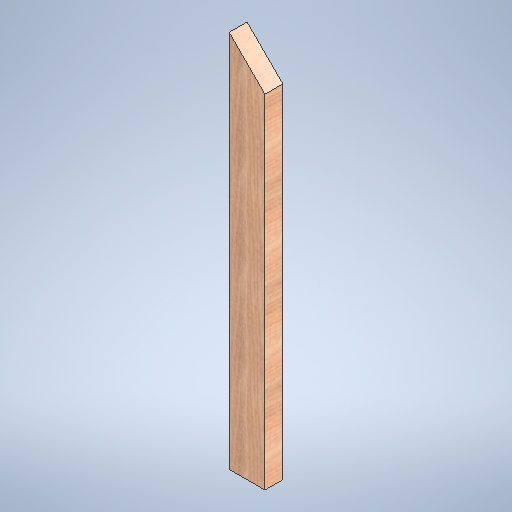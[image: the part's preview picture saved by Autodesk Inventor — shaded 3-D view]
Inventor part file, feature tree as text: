
AUTODESK INVENTOR PART (.ipt)
format: ipt  version: 2025 (Build 290162000, 162)  size: 318,976 bytes
history: native  units: in
note: dims shown in document units (in); Inventor stores cm internally (conversion verified against a paired STEP export)
features: extrude x1, sketch x1
ambient origin geometry x8: Origin, YZ Plane, XZ Plane, XY Plane, X Axis, Y Axis, Z Axis, Center Point
bodies: Solid1 (feature_tree)
feature tree (2):
  extrude  "Extrusion1"  Depth=4.0in
  sketch  "Sketch1"  dims[d0=42.343in d1=4.0in d2=38.343in d3=2.0in d4=0.0in]
